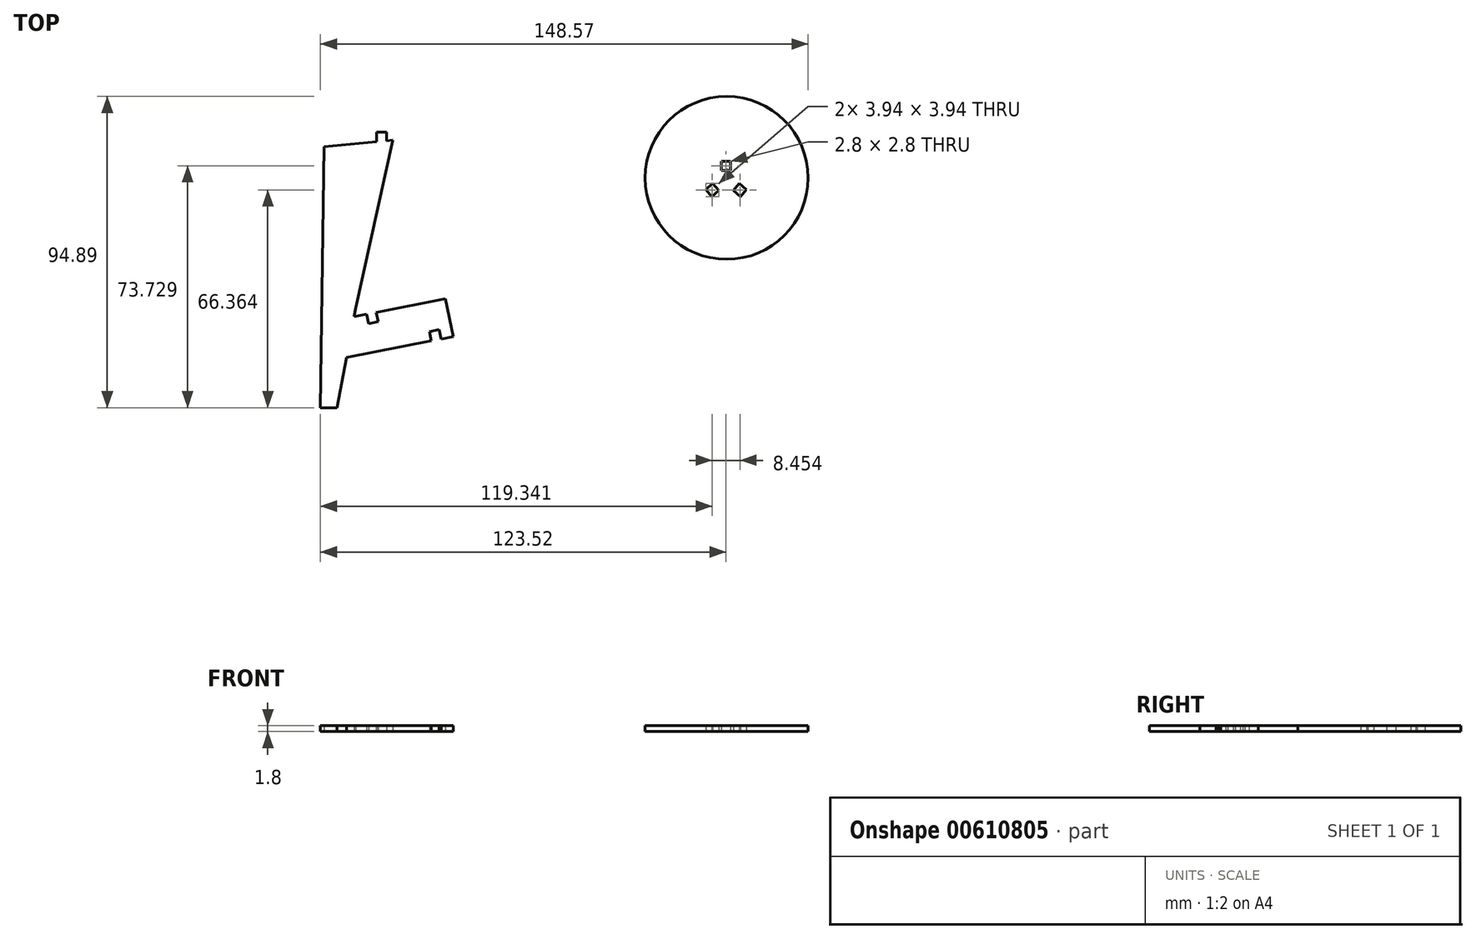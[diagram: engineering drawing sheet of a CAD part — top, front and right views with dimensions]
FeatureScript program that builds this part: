
annotation { "Feature Type Name" : "Feature", "Feature Type Description" : "" }
export const myFeature = defineFeature(function(context is Context, id is Id, definition is map)
    precondition{}
    {
        {
            var Q0;
            Q0=qCreatedBy(makeId("Top.planeOp"),FACE);
            var sketch = newSketch(context, id + "F0", { "sketchPlane" : qUnion([Q0])});
            skLineSegment(sketch, "E0", {"start": v(-36.47, -14.24) * mm, "end": v(-57.53, -18.34) * mm});
            skLineSegment(sketch, "E1", {"start": v(-57.53, -18.34) * mm, "end": v(-56.93, -21.22) * mm});
            skLineSegment(sketch, "E2", {"start": v(-56.93, -21.22) * mm, "end": v(-59.87, -21.83) * mm});
            skLineSegment(sketch, "E3", {"start": v(-59.87, -21.83) * mm, "end": v(-60.48, -18.92) * mm});
            skLineSegment(sketch, "E4", {"start": v(-60.48, -18.92) * mm, "end": v(-64.32, -19.67) * mm});
            skLineSegment(sketch, "E5", {"start": v(-64.32, -19.67) * mm, "end": v(-63.85, -16.99) * mm});
            skLineSegment(sketch, "E6", {"start": v(-63.85, -16.99) * mm, "end": v(-52.42, 34.19) * mm});
            skLineSegment(sketch, "E7", {"start": v(-52.42, 34.19) * mm, "end": v(-54.44, 34) * mm});
            skLineSegment(sketch, "E8", {"start": v(-54.44, 34) * mm, "end": v(-54.44, 36.56) * mm});
            skLineSegment(sketch, "E9", {"start": v(-54.44, 36.56) * mm, "end": v(-57.45, 36.56) * mm});
            skLineSegment(sketch, "E10", {"start": v(-57.45, 36.56) * mm, "end": v(-57.45, 33.72) * mm});
            skLineSegment(sketch, "E11", {"start": v(-57.45, 33.72) * mm, "end": v(-73.45, 32.22) * mm});
            skLineSegment(sketch, "E12", {"start": v(-73.45, 32.22) * mm, "end": v(-74.54, -47.4) * mm});
            skLineSegment(sketch, "E13", {"start": v(-74.54, -47.4) * mm, "end": v(-69.44, -47.4) * mm});
            skLineSegment(sketch, "E14", {"start": v(-69.44, -47.4) * mm, "end": v(-66.55, -32.06) * mm});
            skLineSegment(sketch, "E15", {"start": v(-66.55, -32.06) * mm, "end": v(-40.74, -27.03) * mm});
            skLineSegment(sketch, "E16", {"start": v(-40.74, -27.03) * mm, "end": v(-41.33, -24.18) * mm});
            skLineSegment(sketch, "E17", {"start": v(-41.33, -24.18) * mm, "end": v(-38.4, -23.56) * mm});
            skLineSegment(sketch, "E18", {"start": v(-38.4, -23.56) * mm, "end": v(-37.79, -26.46) * mm});
            skLineSegment(sketch, "E19", {"start": v(-37.79, -26.46) * mm, "end": v(-34.01, -25.72) * mm});
            skLineSegment(sketch, "E20", {"start": v(-34.01, -25.72) * mm, "end": v(-36.47, -14.24) * mm});
            skLineSegment(sketch, "E21", {"start": v(27.71, -7.18) * mm, "end": v(6.65, -11.29) * mm});
            skLineSegment(sketch, "E22", {"start": v(6.65, -11.29) * mm, "end": v(7.25, -14.16) * mm});
            skLineSegment(sketch, "E23", {"start": v(7.25, -14.16) * mm, "end": v(4.3, -14.78) * mm});
            skLineSegment(sketch, "E24", {"start": v(4.3, -14.78) * mm, "end": v(3.7, -11.86) * mm});
            skLineSegment(sketch, "E25", {"start": v(3.7, -11.86) * mm, "end": v(-0.14, -12.6) * mm});
            skLineSegment(sketch, "E26", {"start": v(-0.14, -12.6) * mm, "end": v(0.33, -9.93) * mm});
            skLineSegment(sketch, "E27", {"start": v(0.33, -9.93) * mm, "end": v(11.76, 41.24) * mm});
            skLineSegment(sketch, "E28", {"start": v(11.76, 41.24) * mm, "end": v(9.74, 41.05) * mm});
            skLineSegment(sketch, "E29", {"start": v(9.74, 41.05) * mm, "end": v(9.74, 43.62) * mm});
            skLineSegment(sketch, "E30", {"start": v(9.74, 43.62) * mm, "end": v(6.74, 43.62) * mm});
            skLineSegment(sketch, "E31", {"start": v(6.74, 43.62) * mm, "end": v(6.74, 40.77) * mm});
            skLineSegment(sketch, "E32", {"start": v(6.74, 40.77) * mm, "end": v(-9.27, 39.27) * mm});
            skLineSegment(sketch, "E33", {"start": v(-9.27, 39.27) * mm, "end": v(-10.36, -40.35) * mm});
            skLineSegment(sketch, "E34", {"start": v(-10.36, -40.35) * mm, "end": v(-5.26, -40.35) * mm});
            skLineSegment(sketch, "E35", {"start": v(-5.26, -40.35) * mm, "end": v(-2.37, -25) * mm});
            skLineSegment(sketch, "E36", {"start": v(-2.37, -25) * mm, "end": v(23.45, -19.97) * mm});
            skLineSegment(sketch, "E37", {"start": v(23.45, -19.97) * mm, "end": v(22.85, -17.12) * mm});
            skLineSegment(sketch, "E38", {"start": v(22.85, -17.12) * mm, "end": v(25.79, -16.5) * mm});
            skLineSegment(sketch, "E39", {"start": v(25.79, -16.5) * mm, "end": v(26.4, -19.4) * mm});
            skLineSegment(sketch, "E40", {"start": v(26.4, -19.4) * mm, "end": v(30.17, -18.66) * mm});
            skLineSegment(sketch, "E41", {"start": v(30.17, -18.66) * mm, "end": v(27.71, -7.18) * mm});
            skLineSegment(sketch, "E42", {"start": v(-51.82, 3.4) * mm, "end": v(-30.76, 7.5) * mm});
            skLineSegment(sketch, "E43", {"start": v(-30.76, 7.5) * mm, "end": v(-31.36, 10.38) * mm});
            skLineSegment(sketch, "E44", {"start": v(-31.36, 10.38) * mm, "end": v(-28.42, 11) * mm});
            skLineSegment(sketch, "E45", {"start": v(-28.42, 11) * mm, "end": v(-27.8, 8.08) * mm});
            skLineSegment(sketch, "E46", {"start": v(-27.8, 8.08) * mm, "end": v(-23.97, 8.82) * mm});
            skLineSegment(sketch, "E47", {"start": v(-23.97, 8.82) * mm, "end": v(-24.44, 6.15) * mm});
            skLineSegment(sketch, "E48", {"start": v(-24.44, 6.15) * mm, "end": v(-35.87, -45.03) * mm});
            skLineSegment(sketch, "E49", {"start": v(-35.87, -45.03) * mm, "end": v(-33.85, -44.84) * mm});
            skLineSegment(sketch, "E50", {"start": v(-33.85, -44.84) * mm, "end": v(-33.85, -47.4) * mm});
            skLineSegment(sketch, "E51", {"start": v(-33.85, -47.4) * mm, "end": v(-30.85, -47.4) * mm});
            skLineSegment(sketch, "E52", {"start": v(-30.85, -47.4) * mm, "end": v(-30.85, -44.56) * mm});
            skLineSegment(sketch, "E53", {"start": v(-30.85, -44.56) * mm, "end": v(-14.84, -43.06) * mm});
            skLineSegment(sketch, "E54", {"start": v(-14.84, -43.06) * mm, "end": v(-13.75, 36.56) * mm});
            skLineSegment(sketch, "E55", {"start": v(-13.75, 36.56) * mm, "end": v(-18.85, 36.56) * mm});
            skLineSegment(sketch, "E56", {"start": v(-18.85, 36.56) * mm, "end": v(-21.74, 21.22) * mm});
            skLineSegment(sketch, "E57", {"start": v(-21.74, 21.22) * mm, "end": v(-47.56, 16.19) * mm});
            skLineSegment(sketch, "E58", {"start": v(-47.56, 16.19) * mm, "end": v(-46.96, 13.34) * mm});
            skLineSegment(sketch, "E59", {"start": v(-46.96, 13.34) * mm, "end": v(-49.9, 12.72) * mm});
            skLineSegment(sketch, "E60", {"start": v(-49.9, 12.72) * mm, "end": v(-50.5, 15.61) * mm});
            skLineSegment(sketch, "E61", {"start": v(-50.5, 15.61) * mm, "end": v(-54.28, 14.88) * mm});
            skLineSegment(sketch, "E62", {"start": v(-54.28, 14.88) * mm, "end": v(-51.82, 3.4) * mm});
            skLineSegment(sketch, "E63", {"start": v(50.38, 24.93) * mm, "end": v(47.58, 24.93) * mm});
            skLineSegment(sketch, "E64", {"start": v(47.58, 24.93) * mm, "end": v(47.58, 27.73) * mm});
            skLineSegment(sketch, "E65", {"start": v(47.58, 27.73) * mm, "end": v(50.38, 27.73) * mm});
            skLineSegment(sketch, "E66", {"start": v(50.38, 27.73) * mm, "end": v(50.38, 24.93) * mm});
            skLineSegment(sketch, "E67", {"start": v(46.77, 18.8) * mm, "end": v(44.63, 17) * mm});
            skLineSegment(sketch, "E68", {"start": v(44.63, 17) * mm, "end": v(42.83, 19.14) * mm});
            skLineSegment(sketch, "E69", {"start": v(42.83, 19.14) * mm, "end": v(44.97, 20.94) * mm});
            skLineSegment(sketch, "E70", {"start": v(44.97, 20.94) * mm, "end": v(46.77, 18.8) * mm});
            skLineSegment(sketch, "E71", {"start": v(53.43, 17) * mm, "end": v(51.28, 18.8) * mm});
            skLineSegment(sketch, "E72", {"start": v(51.28, 18.8) * mm, "end": v(53.08, 20.94) * mm});
            skLineSegment(sketch, "E73", {"start": v(53.08, 20.94) * mm, "end": v(55.23, 19.14) * mm});
            skLineSegment(sketch, "E74", {"start": v(55.23, 19.14) * mm, "end": v(53.43, 17) * mm});
            skPoint(sketch, "E75.endSnap0", {"position": v(52.18, 19.86) * mm});
            skCircle(sketch, "E76", {"center": v(49.2, 22.66) * mm, "radius": 24.83 * mm});
            skSolve(sketch);
        }
        {
            var Q0;
            Q0=makeQuery(id+"F0.imprint","IMPRINT",FACE,{"disambiguationData":[TD([[makeQuery(id+"F0.imprint","IMPRINT",EDGE,{"derivedFrom":sQuery(id+"F0.wireOp",EDGE,"E63")}),1.0]])]});
            extrude(context, id + "F1", {"entities" : qUnion([Q0]), "depth" : 1.8 * mm, "offsetDistance" : 25 * mm});
        }
        {
            var Q0;
            Q0=makeQuery(id+"F0.imprint","IMPRINT",FACE,{"disambiguationData":[TD([[makeQuery(id+"F0.imprint","IMPRINT",EDGE,{"derivedFrom":sQuery(id+"F0.wireOp",EDGE,"E0")}),1.0]])]});
            extrude(context, id + "F2", {"entities" : qUnion([Q0]), "depth" : 1.8 * mm, "offsetDistance" : 25 * mm});
        }
    });
